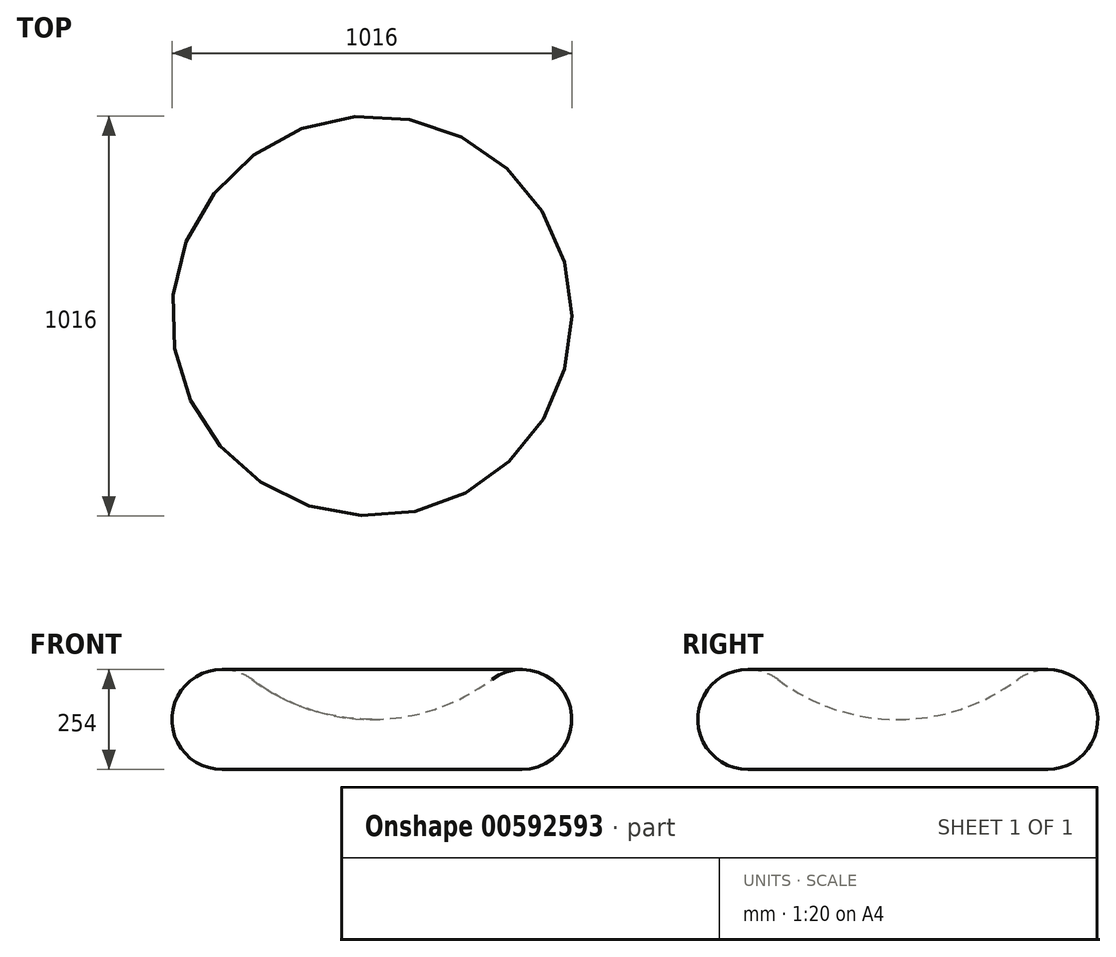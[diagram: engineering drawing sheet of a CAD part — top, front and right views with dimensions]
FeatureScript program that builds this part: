
annotation { "Feature Type Name" : "Feature", "Feature Type Description" : "" }
export const myFeature = defineFeature(function(context is Context, id is Id, definition is map)
    precondition{}
    {
        {
            var Q0;
            Q0=qCreatedBy(makeId("Front.planeOp"),FACE);
            var sketch = newSketch(context, id + "F0", { "sketchPlane" : qUnion([Q0])});
            skArc(sketch, "E0", {"start": v(-304.8, 358.94) * mm, "mid": v(-501.48, 297.5) * mm, "end": v(-381, 130.34) * mm});
            skArc(sketch, "E1", {"start": v(-304.8, 358.94) * mm, "mid": v(-160.64, 283.4) * mm, "end": v(0, 257.34) * mm});
            skLineSegment(sketch, "E2", {"start": v(0, 257.34) * mm, "end": v(0, 130.34) * mm});
            skLineSegment(sketch, "E3", {"start": v(0, 130.34) * mm, "end": v(-381, 130.34) * mm});
            skSolve(sketch);
        }
        {
            var Q0;
            Q0=makeQuery(id+"F0.imprint","IMPRINT",FACE,{"disambiguationData":[TD([[makeQuery(id+"F0.imprint","IMPRINT",EDGE,{"derivedFrom":sQuery(id+"F0.wireOp",EDGE,"E0")}),1.0]])]});
            var Q1;
            Q1=sQuery(id+"F0.wireOp",EDGE,"E2");
            revolve(context, id + "F1", {"entities" : qUnion([Q0]), "axis" : qUnion([Q1]), "revolveType" : RevolveType.FULL});
        }
    });
